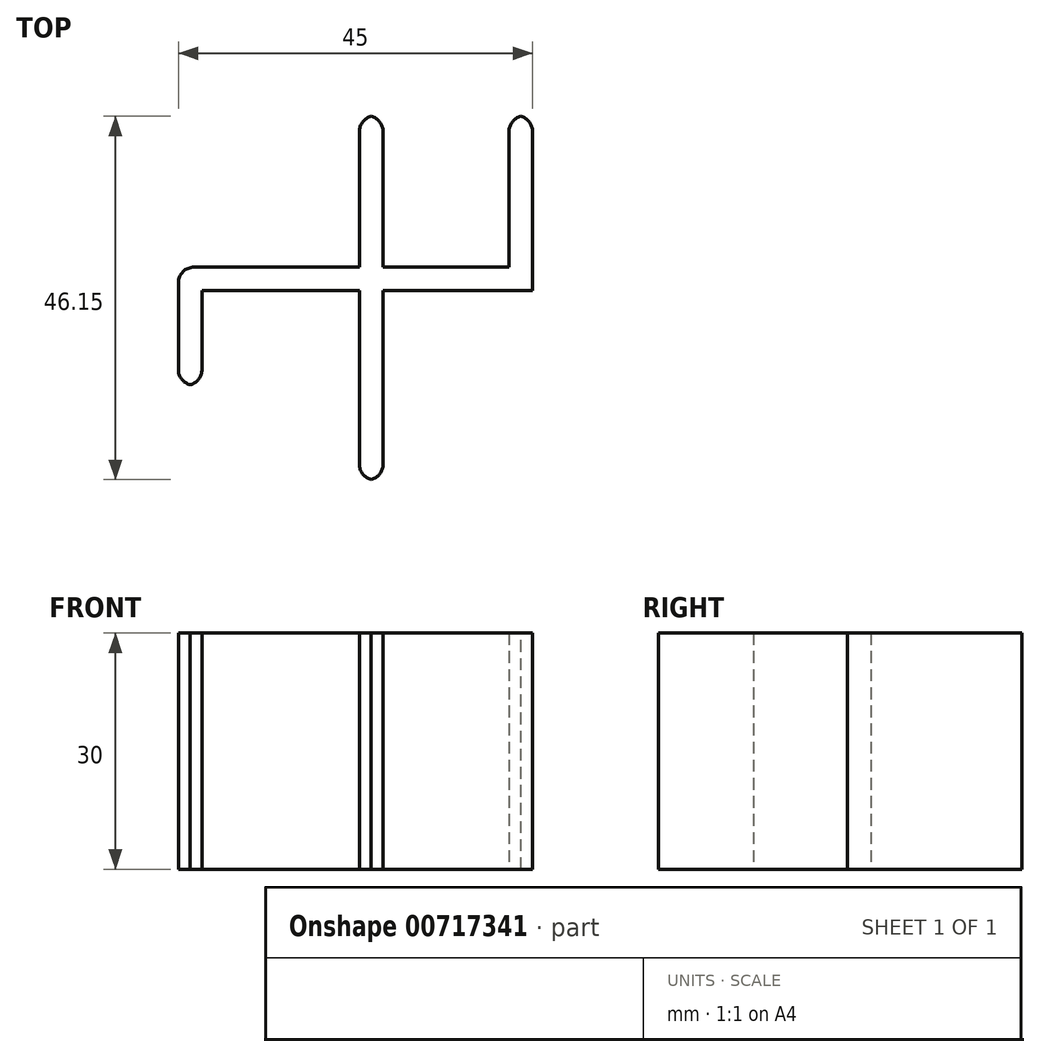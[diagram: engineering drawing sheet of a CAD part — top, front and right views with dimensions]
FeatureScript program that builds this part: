
annotation { "Feature Type Name" : "Feature", "Feature Type Description" : "" }
export const myFeature = defineFeature(function(context is Context, id is Id, definition is map)
    precondition{}
    {
        {
            var Q0;
            Q0=qCreatedBy(makeId("Top.planeOp"),FACE);
            var sketch = newSketch(context, id + "F0", { "sketchPlane" : qUnion([Q0])});
            skLineSegment(sketch, "E0.bottom", {"start": v(-23, 3) * mm, "end": v(-20, 3) * mm});
            skLineSegment(sketch, "E0.top", {"start": v(-23, -12) * mm, "end": v(-20, -12) * mm});
            skLineSegment(sketch, "E0.left", {"start": v(-23, 3) * mm, "end": v(-23, -12) * mm});
            skLineSegment(sketch, "E1.left", {"start": v(3, 0) * mm, "end": v(3, -12) * mm});
            skLineSegment(sketch, "E1.right", {"start": v(0, 0) * mm, "end": v(0, -12) * mm});
            skLineSegment(sketch, "E2.bottom", {"start": v(3, 3) * mm, "end": v(19, 3) * mm});
            skLineSegment(sketch, "E2.top", {"start": v(3, 0) * mm, "end": v(19, 0) * mm});
            skLineSegment(sketch, "E3.left", {"start": v(19, 3) * mm, "end": v(19, 22.22) * mm});
            skLineSegment(sketch, "E4", {"start": v(19, 0) * mm, "end": v(22, 0) * mm});
            skLineSegment(sketch, "E5", {"start": v(22, 0) * mm, "end": v(22, 22.22) * mm});
            skLineSegment(sketch, "E6", {"start": v(22, 22.22) * mm, "end": v(19, 22.22) * mm});
            skLineSegment(sketch, "E7", {"start": v(-20, -12) * mm, "end": v(-20, 0) * mm});
            skLineSegment(sketch, "E8", {"start": v(3, -12) * mm, "end": v(3, 0) * mm});
            skLineSegment(sketch, "E9", {"start": v(19, 22.22) * mm, "end": v(19, 3) * mm});
            skLineSegment(sketch, "E10", {"start": v(0, 0) * mm, "end": v(-20, 0) * mm});
            skLineSegment(sketch, "E11", {"start": v(0, -12) * mm, "end": v(0, -24.05) * mm});
            skLineSegment(sketch, "E12", {"start": v(0, -24.05) * mm, "end": v(3, -24.05) * mm});
            skLineSegment(sketch, "E13", {"start": v(3, -24.05) * mm, "end": v(3, -12) * mm});
            skLineSegment(sketch, "E14", {"start": v(3, 3) * mm, "end": v(3, 22.22) * mm});
            skLineSegment(sketch, "E15", {"start": v(3, 22.22) * mm, "end": v(0, 22.22) * mm});
            skLineSegment(sketch, "E16", {"start": v(0, 22.22) * mm, "end": v(0, 3) * mm});
            skLineSegment(sketch, "E17", {"start": v(0, 3) * mm, "end": v(-20, 3) * mm});
            skSolve(sketch);
        }
        {
            var Q0;
            Q0=makeQuery(id+"F0.imprint","IMPRINT",FACE,{"disambiguationData":[TD([[makeQuery(id+"F0.imprint","IMPRINT",EDGE,{"derivedFrom":sQuery(id+"F0.wireOp",EDGE,"E0.bottom")}),-1.0]])]});
            extrude(context, id + "F1", {"entities" : qUnion([Q0]), "depth" : 30 * mm, "offsetDistance" : 25 * mm});
        }
        {
            var Q0;
            Q0=makeQuery(id+"F1.opExtrude","SWEPT_EDGE",EDGE,{"disambiguationData":[OSD([sQuery(id+"F0.wireOp",EDGE,"E11"),sQuery(id+"F0.wireOp",EDGE,"E12")])]});
            var Q1;
            Q1=makeQuery(id+"F1.opExtrude","SWEPT_EDGE",EDGE,{"disambiguationData":[OSD([sQuery(id+"F0.wireOp",EDGE,"E12"),sQuery(id+"F0.wireOp",EDGE,"E13")])]});
            fillet(context, id + "F2", {"entities" : qUnion([Q0, Q1]), "radius" : 2 * mm, "tangentPropagation" : true, "allowEdgeOverflow" : false});
        }
        {
            var Q0;
            Q0=makeQuery(id+"F1.opExtrude","SWEPT_EDGE",EDGE,{"disambiguationData":[OSD([sQuery(id+"F0.wireOp",EDGE,"E0.top"),sQuery(id+"F0.wireOp",EDGE,"E0.left")])]});
            var Q1;
            Q1=makeQuery(id+"F1.opExtrude","SWEPT_EDGE",EDGE,{"disambiguationData":[OSD([sQuery(id+"F0.wireOp",EDGE,"E0.top"),sQuery(id+"F0.wireOp",EDGE,"E7")])]});
            fillet(context, id + "F3", {"entities" : qUnion([Q0, Q1]), "radius" : 2 * mm, "tangentPropagation" : true, "allowEdgeOverflow" : false});
        }
        {
            var Q0;
            Q0=makeQuery(id+"F1.opExtrude","SWEPT_EDGE",EDGE,{"disambiguationData":[OSD([sQuery(id+"F0.wireOp",EDGE,"E0.bottom"),sQuery(id+"F0.wireOp",EDGE,"E0.left")])]});
            var Q1;
            Q1=makeQuery(id+"F1.opExtrude","SWEPT_EDGE",EDGE,{"disambiguationData":[OSD([sQuery(id+"F0.wireOp",EDGE,"E15"),sQuery(id+"F0.wireOp",EDGE,"E16")])]});
            var Q2;
            Q2=makeQuery(id+"F1.opExtrude","SWEPT_EDGE",EDGE,{"disambiguationData":[OSD([sQuery(id+"F0.wireOp",EDGE,"E6"),sQuery(id+"F0.wireOp",EDGE,"E9")])]});
            var Q3;
            Q3=makeQuery(id+"F1.opExtrude","SWEPT_EDGE",EDGE,{"disambiguationData":[OSD([sQuery(id+"F0.wireOp",EDGE,"E14"),sQuery(id+"F0.wireOp",EDGE,"E15")])]});
            var Q4;
            Q4=makeQuery(id+"F1.opExtrude","SWEPT_EDGE",EDGE,{"disambiguationData":[OSD([sQuery(id+"F0.wireOp",EDGE,"E6"),sQuery(id+"F0.wireOp",EDGE,"E5")])]});
            fillet(context, id + "F4", {"entities" : qUnion([Q0, Q1, Q2, Q3, Q4]), "radius" : 2 * mm, "tangentPropagation" : true, "allowEdgeOverflow" : false});
        }
    });
